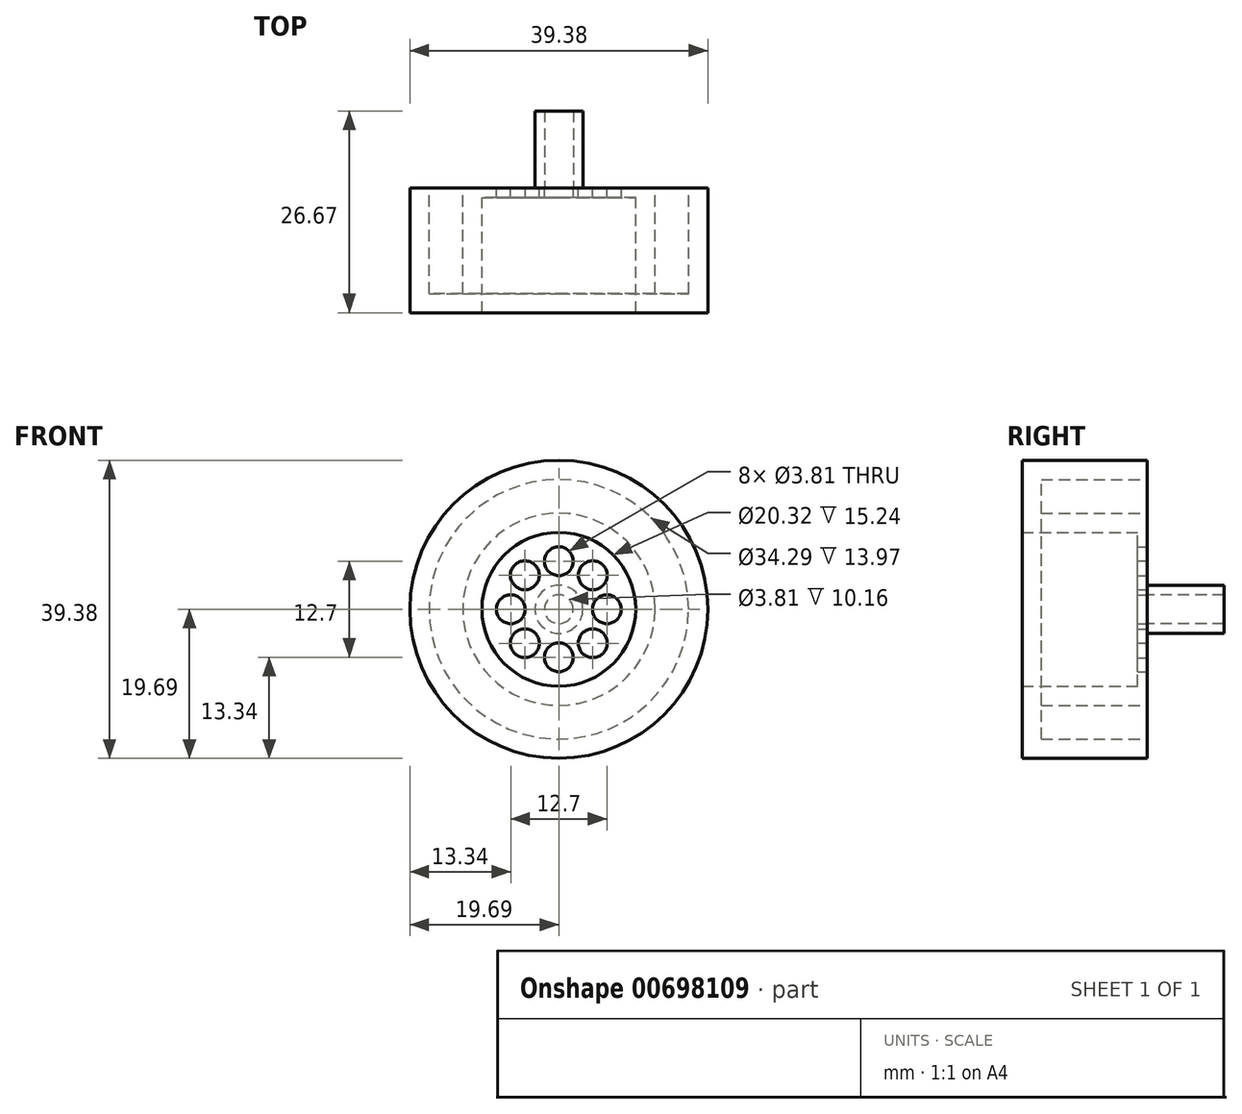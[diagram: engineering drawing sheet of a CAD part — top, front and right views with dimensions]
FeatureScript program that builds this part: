
annotation { "Feature Type Name" : "Feature", "Feature Type Description" : "" }
export const myFeature = defineFeature(function(context is Context, id is Id, definition is map)
    precondition{}
    {
        {
            var Q0;
            Q0=qCreatedBy(makeId("Front.planeOp"),FACE);
            var sketch = newSketch(context, id + "F0", { "sketchPlane" : qUnion([Q0])});
            skCircle(sketch, "E0", {"center": v(0, 0) * mm, "radius": 19.69 * mm});
            skCircle(sketch, "E1", {"center": v(0, 0) * mm, "radius": 10.16 * mm});
            skCircle(sketch, "E2", {"center": v(0, 0) * mm, "radius": 1.9 * mm});
            skCircle(sketch, "E3", {"center": v(0, 0) * mm, "radius": 3.18 * mm});
            skCircle(sketch, "E4", {"center": v(0, 6.35) * mm, "radius": 1.9 * mm});
            skCircle(sketch, "E5", {"center": v(-6.35, 0) * mm, "radius": 1.9 * mm});
            skCircle(sketch, "E6", {"center": v(0, -6.35) * mm, "radius": 1.9 * mm});
            skCircle(sketch, "E7", {"center": v(6.35, 0) * mm, "radius": 1.9 * mm});
            skCircle(sketch, "E8", {"center": v(-4.5, -4.5) * mm, "radius": 1.9 * mm});
            skCircle(sketch, "E9", {"center": v(4.5, 4.5) * mm, "radius": 1.9 * mm});
            skCircle(sketch, "E10", {"center": v(-4.5, 4.5) * mm, "radius": 1.9 * mm});
            skCircle(sketch, "E11", {"center": v(4.5, -4.5) * mm, "radius": 1.9 * mm});
            skSolve(sketch);
        }
        {
            var Q0;
            Q0=makeQuery(id+"F0.imprint","IMPRINT",FACE,{"disambiguationData":[TD([[makeQuery(id+"F0.imprint","IMPRINT",EDGE,{"derivedFrom":sQuery(id+"F0.wireOp",EDGE,"E0")}),1.0]])]});
            extrude(context, id + "F1", {"entities" : qUnion([Q0]), "depth" : 16.5 * mm, "offsetDistance" : 25.4 * mm});
        }
        {
            var Q0;
            Q0=makeQuery(id+"F0.imprint","IMPRINT",FACE,{"disambiguationData":[TD([[makeQuery(id+"F0.imprint","IMPRINT",EDGE,{"derivedFrom":sQuery(id+"F0.wireOp",EDGE,"E0")}),1.0]])]});
            var sketch = newSketch(context, id + "F2", { "sketchPlane" : qUnion([Q0])});
            skCircle(sketch, "E12.0", {"center": v(0, 0) * mm, "radius": 18.41 * mm});
            skSolve(sketch);
        }
        {
            var Q0;
            Q0=makeQuery(id+"F1.opExtrude","CAP_FACE",FACE,{"disambiguationData":[OSD([sQuery(id+"F0.wireOp",EDGE,"E0"),sQuery(id+"F0.wireOp",EDGE,"E1")])],"isStart":true});
            shell(context, id + "F3", {"entities" : qUnion([Q0]), "thickness" : 2.54 * mm});
        }
        {
            var Q0;
            Q0=makeQuery(id+"F2.imprint","IMPRINT",FACE,{"disambiguationData":[TD([[makeQuery(id+"F2.imprint","IMPRINT",EDGE,{"derivedFrom":makeQuery(id+"F0.imprint","IMPRINT",EDGE,{"derivedFrom":sQuery(id+"F0.wireOp",EDGE,"E1")})}),1.0]])]});
            extrude(context, id + "F4", {"entities" : qUnion([Q0]), "operationType" : NewBodyOperationType.ADD, "depth" : 1.27 * mm, "offsetDistance" : 25.4 * mm});
        }
        {
            var Q0;
            Q0=makeQuery(id+"F0.imprint","IMPRINT",FACE,{"disambiguationData":[TD([[makeQuery(id+"F0.imprint","IMPRINT",EDGE,{"derivedFrom":sQuery(id+"F0.wireOp",EDGE,"E9")}),1.0]])]});
            var Q1;
            Q1=makeQuery(id+"F0.imprint","IMPRINT",FACE,{"disambiguationData":[TD([[makeQuery(id+"F0.imprint","IMPRINT",EDGE,{"derivedFrom":sQuery(id+"F0.wireOp",EDGE,"E7")}),1.0]])]});
            var Q2;
            Q2=makeQuery(id+"F0.imprint","IMPRINT",FACE,{"disambiguationData":[TD([[makeQuery(id+"F0.imprint","IMPRINT",EDGE,{"derivedFrom":sQuery(id+"F0.wireOp",EDGE,"E11")}),1.0]])]});
            var Q3;
            Q3=makeQuery(id+"F0.imprint","IMPRINT",FACE,{"disambiguationData":[TD([[makeQuery(id+"F0.imprint","IMPRINT",EDGE,{"derivedFrom":sQuery(id+"F0.wireOp",EDGE,"E6")}),1.0]])]});
            var Q4;
            Q4=makeQuery(id+"F0.imprint","IMPRINT",FACE,{"disambiguationData":[TD([[makeQuery(id+"F0.imprint","IMPRINT",EDGE,{"derivedFrom":sQuery(id+"F0.wireOp",EDGE,"E8")}),1.0]])]});
            var Q5;
            Q5=makeQuery(id+"F0.imprint","IMPRINT",FACE,{"disambiguationData":[TD([[makeQuery(id+"F0.imprint","IMPRINT",EDGE,{"derivedFrom":sQuery(id+"F0.wireOp",EDGE,"E5")}),1.0]])]});
            var Q6;
            Q6=makeQuery(id+"F0.imprint","IMPRINT",FACE,{"disambiguationData":[TD([[makeQuery(id+"F0.imprint","IMPRINT",EDGE,{"derivedFrom":sQuery(id+"F0.wireOp",EDGE,"E10")}),1.0]])]});
            var Q7;
            Q7=makeQuery(id+"F0.imprint","IMPRINT",FACE,{"disambiguationData":[TD([[makeQuery(id+"F0.imprint","IMPRINT",EDGE,{"derivedFrom":sQuery(id+"F0.wireOp",EDGE,"E4")}),1.0]])]});
            extrude(context, id + "F5", {"entities" : qUnion([Q0, Q1, Q2, Q3, Q4, Q5, Q6, Q7]), "operationType" : NewBodyOperationType.REMOVE, "depth" : 25.4 * mm, "offsetDistance" : 25.4 * mm});
        }
        {
            var Q0;
            Q0=makeQuery(id+"F0.imprint","IMPRINT",FACE,{"disambiguationData":[TD([[makeQuery(id+"F0.imprint","IMPRINT",EDGE,{"derivedFrom":sQuery(id+"F0.wireOp",EDGE,"E2")}),-1.0]])]});
            extrude(context, id + "F6", {"entities" : qUnion([Q0]), "operationType" : NewBodyOperationType.ADD, "oppositeDirection" : true, "depth" : 10.16 * mm, "offsetDistance" : 25.4 * mm});
        }
    });
